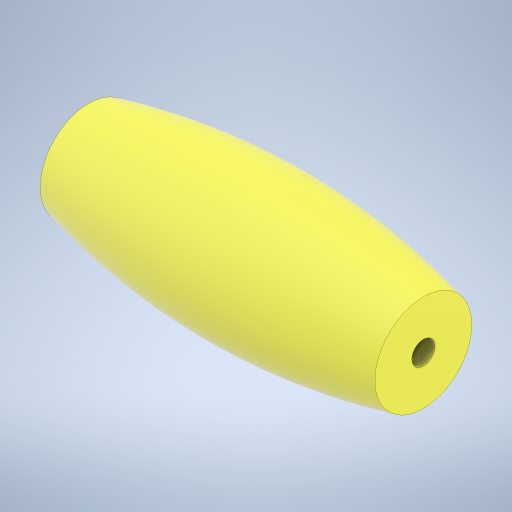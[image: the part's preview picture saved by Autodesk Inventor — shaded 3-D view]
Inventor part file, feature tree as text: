
AUTODESK INVENTOR PART (.ipt)
format: ipt  version: 2024.2 (Build 282272000, 272)  size: 266,240 bytes
history: native  units: mm
features: sketch x2, revolve x1, hole x1
ambient origin geometry x8: Origin, YZ Plane, XZ Plane, XY Plane, X Axis, Y Axis, Z Axis, Center Point
bodies: Solid1 (feature_tree)
feature tree (4):
  revolve  "Revolution1"  [1 undecoded]
  hole  "Hole1"  [1 undecoded]
  sketch  "Sketch1"  dims[d0=12.0mm d1=29.0mm]
  sketch  "Sketch2"  dims[d2=59.0mm d3=90.0deg d4=2.0mm d5=6.0mm d6=4.0mm d7=2.0mm d8=90.0deg d9=8.0mm d10=20.594885mm]
note: 2 required parameter values undecoded (feature->parameter linkage not recoverable at this tier; creation-order binding heuristic only, values carry confidence <= 0.55)